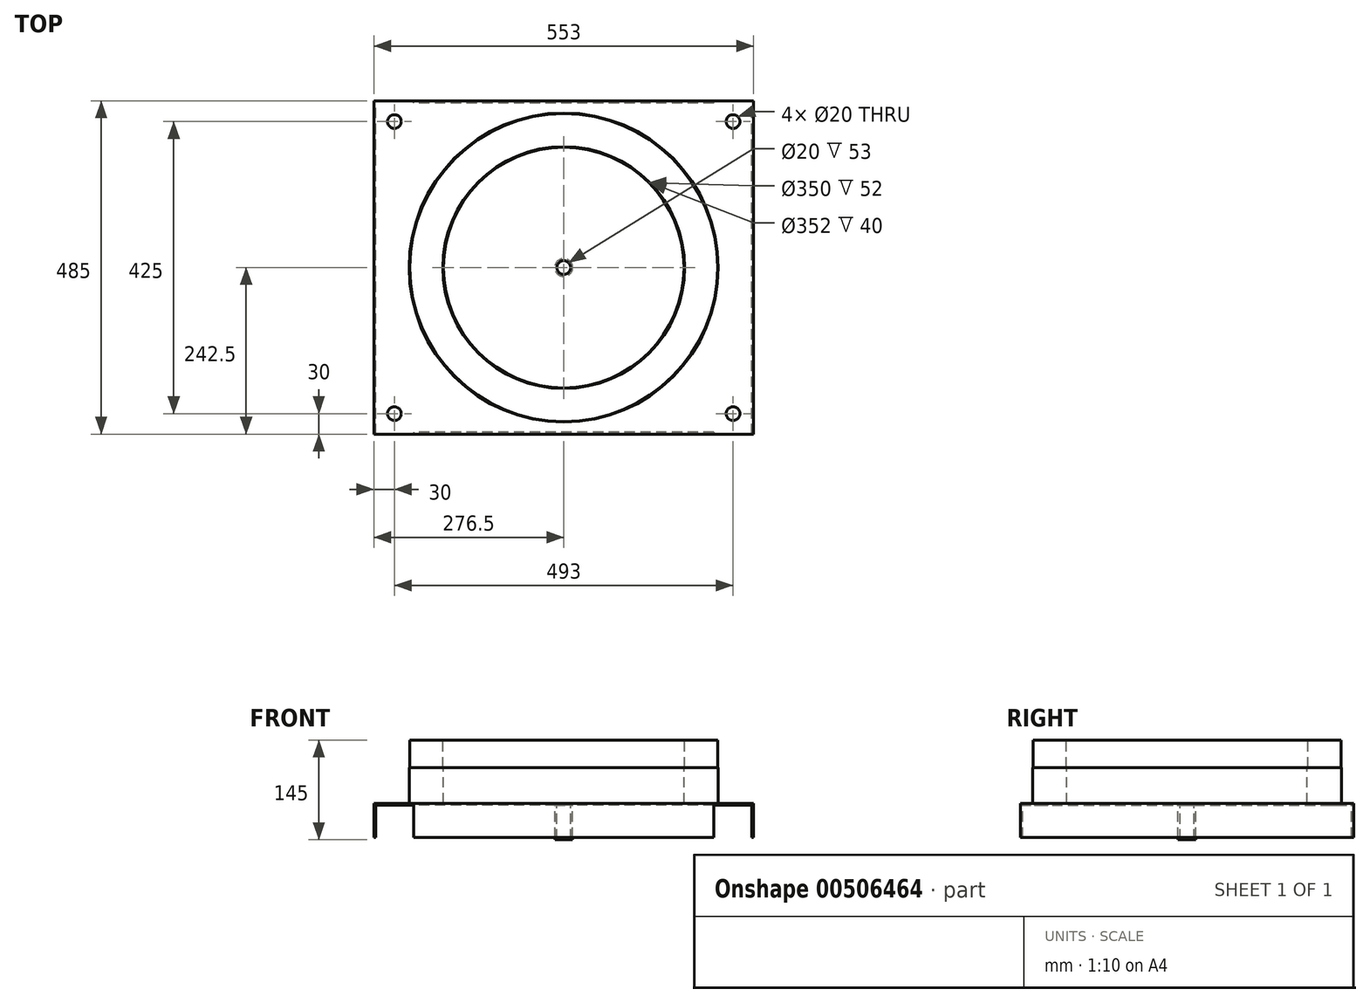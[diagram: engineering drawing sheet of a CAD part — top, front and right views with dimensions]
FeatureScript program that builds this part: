
annotation { "Feature Type Name" : "Feature", "Feature Type Description" : "" }
export const myFeature = defineFeature(function(context is Context, id is Id, definition is map)
    precondition{}
    {
        {
            var Q0;
            Q0=qCreatedBy(makeId("Front.planeOp"),FACE);
            var sketch = newSketch(context, id + "F0", { "sketchPlane" : qUnion([Q0])});
            skLineSegment(sketch, "E0", {"start": v(0, 74.87) * mm, "end": v(0, -73.71) * mm, "construction": true});
            skLineSegment(sketch, "E1", {"start": v(0, 374.84) * mm, "end": v(0, 1) * mm, "construction": true});
            skLineSegment(sketch, "E2", {"start": v(-175, 3) * mm, "end": v(-175, 55) * mm});
            skLineSegment(sketch, "E3", {"start": v(-175, 55) * mm, "end": v(-176, 55) * mm});
            skLineSegment(sketch, "E4", {"start": v(-176, 55) * mm, "end": v(-176, 95) * mm});
            skLineSegment(sketch, "E5", {"start": v(-176, 95) * mm, "end": v(-224, 95) * mm});
            skLineSegment(sketch, "E6", {"start": v(-224, 95) * mm, "end": v(-224, 55) * mm});
            skLineSegment(sketch, "E7", {"start": v(-224, 55) * mm, "end": v(-225, 55) * mm});
            skLineSegment(sketch, "E8", {"start": v(-225, 55) * mm, "end": v(-225, 3) * mm});
            skLineSegment(sketch, "E9", {"start": v(-225, 3) * mm, "end": v(-175, 3) * mm});
            skLineSegment(sketch, "E10.trimOffspring", {"start": v(0, 0) * mm, "end": v(0, -528.94) * mm, "construction": true});
            skLineSegment(sketch, "E11.bottom", {"start": v(-225, 3) * mm, "end": v(-10, 3) * mm});
            skLineSegment(sketch, "E11.top", {"start": v(-225, 0) * mm, "end": v(-10, 0) * mm});
            skLineSegment(sketch, "E11.left", {"start": v(-225, 3) * mm, "end": v(-225, 0) * mm});
            skLineSegment(sketch, "E11.right", {"start": v(-10, 3) * mm, "end": v(-10, 0) * mm});
            skSolve(sketch);
        }
        {
            var Q0;
            Q0=qSketchRegion(id+"F0",true);
            var Q1;
            Q1=sQuery(id+"F0.wireOp",EDGE,"E1");
            revolve(context, id + "F1", {"entities" : qUnion([Q0]), "axis" : qUnion([Q1]), "revolveType" : RevolveType.FULL});
        }
        {
            var Q0;
            Q0=qCreatedBy(makeId("Top.planeOp"),FACE);
            var sketch = newSketch(context, id + "F2", { "sketchPlane" : qUnion([Q0])});
            skLineSegment(sketch, "E12.bottom", {"start": v(276.5, 242.5) * mm, "end": v(-276.5, 242.5) * mm});
            skLineSegment(sketch, "E12.top", {"start": v(276.5, -242.5) * mm, "end": v(-276.5, -242.5) * mm});
            skLineSegment(sketch, "E12.left", {"start": v(276.5, 242.5) * mm, "end": v(276.5, -242.5) * mm});
            skLineSegment(sketch, "E12.right", {"start": v(-276.5, 242.5) * mm, "end": v(-276.5, -242.5) * mm});
            skPoint(sketch, "E12.middle", {"position": v(0, 0) * mm});
            skCircle(sketch, "E13.0", {"center": v(0, 0) * mm, "radius": 176 * mm});
            skCircle(sketch, "E14.0", {"center": v(0, 0) * mm, "radius": 175 * mm});
            skCircle(sketch, "E15", {"center": v(0, 0) * mm, "radius": 200 * mm});
            skLineSegment(sketch, "E16", {"start": v(0, 0) * mm, "end": v(0, 773.78) * mm, "construction": true});
            skLineSegment(sketch, "E17", {"start": v(0, 0) * mm, "end": v(1007.48, 0) * mm, "construction": true});
            skCircle(sketch, "E18", {"center": v(246.5, 212.5) * mm, "radius": 10 * mm});
            skCircle(sketch, "E19.MirrorC", {"center": v(-246.5, 212.5) * mm, "radius": 10 * mm});
            skCircle(sketch, "E20.MirrorC", {"center": v(246.5, -212.5) * mm, "radius": 10 * mm});
            skCircle(sketch, "E21.MirrorC", {"center": v(-246.5, -212.5) * mm, "radius": 10 * mm});
            skSolve(sketch);
        }
        {
            var Q0;
            Q0=qSketchRegion(id+"F2",true);
            extrude(context, id + "F3", {"entities" : qUnion([Q0]), "operationType" : NewBodyOperationType.ADD, "depth" : 3 * mm, "offsetDistance" : 25 * mm});
        }
        {
            var Q0;
            Q0=makeQuery(id+"F3.opExtrude","CAP_FACE",FACE,{"disambiguationData":[OSD([sQuery(id+"F2.wireOp",EDGE,"E12.bottom"),sQuery(id+"F2.wireOp",EDGE,"E12.top"),sQuery(id+"F2.wireOp",EDGE,"E12.left"),sQuery(id+"F2.wireOp",EDGE,"E12.right"),sQuery(id+"F2.wireOp",EDGE,"E15"),sQuery(id+"F2.wireOp",EDGE,"E18"),sQuery(id+"F2.wireOp",EDGE,"E19.MirrorC"),sQuery(id+"F2.wireOp",EDGE,"E20.MirrorC"),sQuery(id+"F2.wireOp",EDGE,"E21.MirrorC")])],"isStart":false});
            var sketch = newSketch(context, id + "F4", { "sketchPlane" : qUnion([Q0])});
            skLineSegment(sketch, "E22", {"start": v(0, 0) * mm, "end": v(-1098.02, 0) * mm, "construction": true});
            skLineSegment(sketch, "E23", {"start": v(0, 0) * mm, "end": v(0, -1084.2) * mm, "construction": true});
            skLineSegment(sketch, "E24.bottom", {"start": v(-276.5, -242.5) * mm, "end": v(-273.5, -242.5) * mm});
            skLineSegment(sketch, "E24.top", {"start": v(-276.5, 242.5) * mm, "end": v(-273.5, 242.5) * mm});
            skLineSegment(sketch, "E24.left", {"start": v(-276.5, 242.5) * mm, "end": v(-276.5, -242.5) * mm});
            skLineSegment(sketch, "E24.right", {"start": v(-273.5, 242.5) * mm, "end": v(-273.5, -242.5) * mm});
            skLineSegment(sketch, "E25.MirrorCS", {"start": v(276.5, 242.5) * mm, "end": v(273.5, 242.5) * mm});
            skLineSegment(sketch, "E26.MirrorCS", {"start": v(276.5, -242.5) * mm, "end": v(273.5, -242.5) * mm});
            skLineSegment(sketch, "E27.MirrorCS", {"start": v(276.5, 242.5) * mm, "end": v(276.5, -242.5) * mm});
            skLineSegment(sketch, "E28.MirrorCS", {"start": v(273.5, 242.5) * mm, "end": v(273.5, -242.5) * mm});
            skLineSegment(sketch, "E29.MirrorCS", {"start": v(0, 0) * mm, "end": v(1098.02, 0) * mm, "construction": true});
            skLineSegment(sketch, "E30.bottom", {"start": v(-218.5, -242.5) * mm, "end": v(218.5, -242.5) * mm});
            skLineSegment(sketch, "E30.top", {"start": v(-218.5, -239.5) * mm, "end": v(218.5, -239.5) * mm});
            skLineSegment(sketch, "E30.left", {"start": v(-218.5, -242.5) * mm, "end": v(-218.5, -239.5) * mm});
            skLineSegment(sketch, "E30.right", {"start": v(218.5, -242.5) * mm, "end": v(218.5, -239.5) * mm});
            skLineSegment(sketch, "E31.MirrorCS", {"start": v(-218.5, 242.5) * mm, "end": v(-218.5, 239.5) * mm});
            skLineSegment(sketch, "E32.MirrorCS", {"start": v(218.5, 242.5) * mm, "end": v(218.5, 239.5) * mm});
            skLineSegment(sketch, "E33.MirrorCS", {"start": v(-218.5, 242.5) * mm, "end": v(218.5, 242.5) * mm});
            skLineSegment(sketch, "E34.MirrorCS", {"start": v(-218.5, 239.5) * mm, "end": v(218.5, 239.5) * mm});
            skSolve(sketch);
        }
        {
            var Q0;
            Q0=qSketchRegion(id+"F4",true);
            extrude(context, id + "F5", {"entities" : qUnion([Q0]), "operationType" : NewBodyOperationType.ADD, "oppositeDirection" : true, "depth" : 50 * mm, "offsetDistance" : 25 * mm});
        }
        {
            var Q0;
            Q0=makeQuery(id+"F3.boolean.opBoolean","MERGE",FACE,{"derivedFrom":[makeQuery(id+"F1.opRevolve","SWEPT_FACE",FACE,{"disambiguationData":[OSD([sQuery(id+"F0.wireOp",EDGE,"E11.top")])]}),makeQuery(id+"F3.opExtrude","CAP_FACE",FACE,{"disambiguationData":[OSD([sQuery(id+"F2.wireOp",EDGE,"E12.bottom"),sQuery(id+"F2.wireOp",EDGE,"E12.top"),sQuery(id+"F2.wireOp",EDGE,"E12.left"),sQuery(id+"F2.wireOp",EDGE,"E12.right"),sQuery(id+"F2.wireOp",EDGE,"E13.0"),sQuery(id+"F2.wireOp",EDGE,"E18"),sQuery(id+"F2.wireOp",EDGE,"E19.MirrorC"),sQuery(id+"F2.wireOp",EDGE,"E20.MirrorC"),sQuery(id+"F2.wireOp",EDGE,"E21.MirrorC")])],"isStart":false})]});
            var sketch = newSketch(context, id + "F6", { "sketchPlane" : qUnion([Q0])});
            skCircle(sketch, "E35.0", {"center": v(0, 0) * mm, "radius": 10 * mm});
            skCircle(sketch, "E36", {"center": v(0, 0) * mm, "radius": 13 * mm});
            skSolve(sketch);
        }
        {
            var Q0;
            Q0=qSketchRegion(id+"F6",true);
            extrude(context, id + "F7", {"entities" : qUnion([Q0]), "operationType" : NewBodyOperationType.ADD, "depth" : 50 * mm, "offsetDistance" : 25 * mm});
        }
    });
